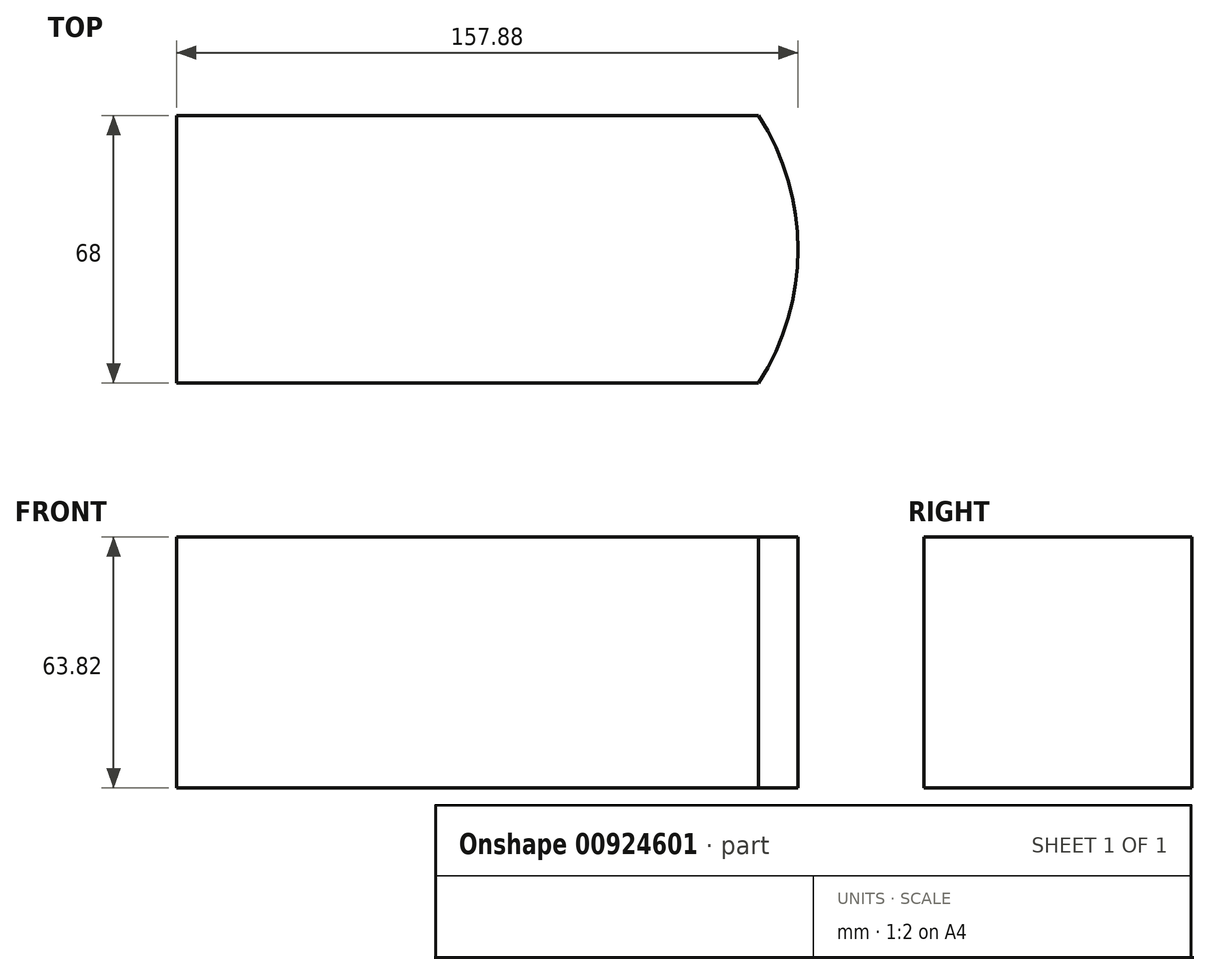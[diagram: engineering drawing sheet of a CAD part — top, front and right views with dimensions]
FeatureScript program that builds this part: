
annotation { "Feature Type Name" : "Feature", "Feature Type Description" : "" }
export const myFeature = defineFeature(function(context is Context, id is Id, definition is map)
    precondition{}
    {
        {
            var Q0;
            Q0=qCreatedBy(makeId("Front.planeOp"),FACE);
            var sketch = newSketch(context, id + "F0", { "sketchPlane" : qUnion([Q0])});
            skLineSegment(sketch, "E0", {"start": v(-31.74, 15.58) * mm, "end": v(-31.74, 78.47) * mm, "construction": true});
            skLineSegment(sketch, "E1.0", {"start": v(62.76, 15.58) * mm, "end": v(62.76, 78.47) * mm, "construction": true});
            skLineSegment(sketch, "E2", {"start": v(107.8, 24.66) * mm, "end": v(-156.8, 24.66) * mm, "construction": true});
            skLineSegment(sketch, "E3", {"start": v(41.75, 35.48) * mm, "end": v(-135.53, 35.48) * mm, "construction": true});
            skLineSegment(sketch, "E4", {"start": v(-38.12, 98.93) * mm, "end": v(-153.45, 98.93) * mm, "construction": true});
            skLineSegment(sketch, "E5", {"start": v(-59.77, 59.74) * mm, "end": v(-59.77, 147.45) * mm, "construction": true});
            skLineSegment(sketch, "E6", {"start": v(98.1, 53.02) * mm, "end": v(98.1, 142.97) * mm, "construction": true});
            skLineSegment(sketch, "E7.bottom", {"start": v(-59.77, 98.93) * mm, "end": v(98.1, 98.93) * mm});
            skLineSegment(sketch, "E7.top", {"start": v(-59.77, 35.1) * mm, "end": v(98.1, 35.1) * mm});
            skLineSegment(sketch, "E7.left", {"start": v(-59.77, 98.93) * mm, "end": v(-59.77, 35.1) * mm});
            skLineSegment(sketch, "E7.right", {"start": v(98.1, 98.93) * mm, "end": v(98.1, 35.1) * mm});
            skSolve(sketch);
        }
        {
            var Q0;
            Q0=makeQuery(id+"F0.imprint","IMPRINT",FACE,{"disambiguationData":[TD([[makeQuery(id+"F0.imprint","IMPRINT",EDGE,{"derivedFrom":sQuery(id+"F0.wireOp",EDGE,"E7.bottom")}),-1.0]])]});
            extrude(context, id + "F1", {"entities" : qUnion([Q0]), "endBound" : BoundingType.SYMMETRIC, "depth" : 68 * mm, "offsetDistance" : 25 * mm});
        }
        {
            var Q0;
            Q0=makeQuery(id+"F1.opExtrude","SWEPT_FACE",FACE,{"disambiguationData":[OSD([sQuery(id+"F0.wireOp",EDGE,"E7.bottom")])]});
            var sketch = newSketch(context, id + "F2", { "sketchPlane" : qUnion([Q0])});
            skLineSegment(sketch, "E8.0", {"start": v(-59.77, -34) * mm, "end": v(88.1, -34) * mm});
            skLineSegment(sketch, "E9.0", {"start": v(-59.77, -34) * mm, "end": v(-59.77, 34) * mm});
            skLineSegment(sketch, "E10.0", {"start": v(-59.77, 34) * mm, "end": v(88.1, 34) * mm});
            skPoint(sketch, "E11.0", {"position": v(98.1, 0) * mm});
            skLineSegment(sketch, "E12.0", {"start": v(98.1, -34) * mm, "end": v(98.1, 34) * mm, "construction": true});
            skLineSegment(sketch, "E13.0", {"start": v(88.1, -34) * mm, "end": v(88.1, 34) * mm, "construction": true});
            skArc(sketch, "E14", {"start": v(88.1, -34) * mm, "mid": v(98.1, 0) * mm, "end": v(88.1, 34) * mm});
            skSolve(sketch);
        }
        {
            var Q0;
            {var subQ1=sQuery(id+"F2.wireOp",EDGE,"E8.0");Q0=makeQuery(id+"F2.imprint","IMPRINT",FACE,{"disambiguationData":[TD([[makeQuery(id+"F2.imprint","IMPRINT",EDGE,{"derivedFrom":subQ1}),1.0]])]});}
            extrude(context, id + "F3", {"entities" : qUnion([Q0]), "operationType" : NewBodyOperationType.INTERSECT, "endBound" : BoundingType.UP_TO_NEXT, "oppositeDirection" : true, "depth" : 25 * mm, "offsetDistance" : 25 * mm});
        }
    });
